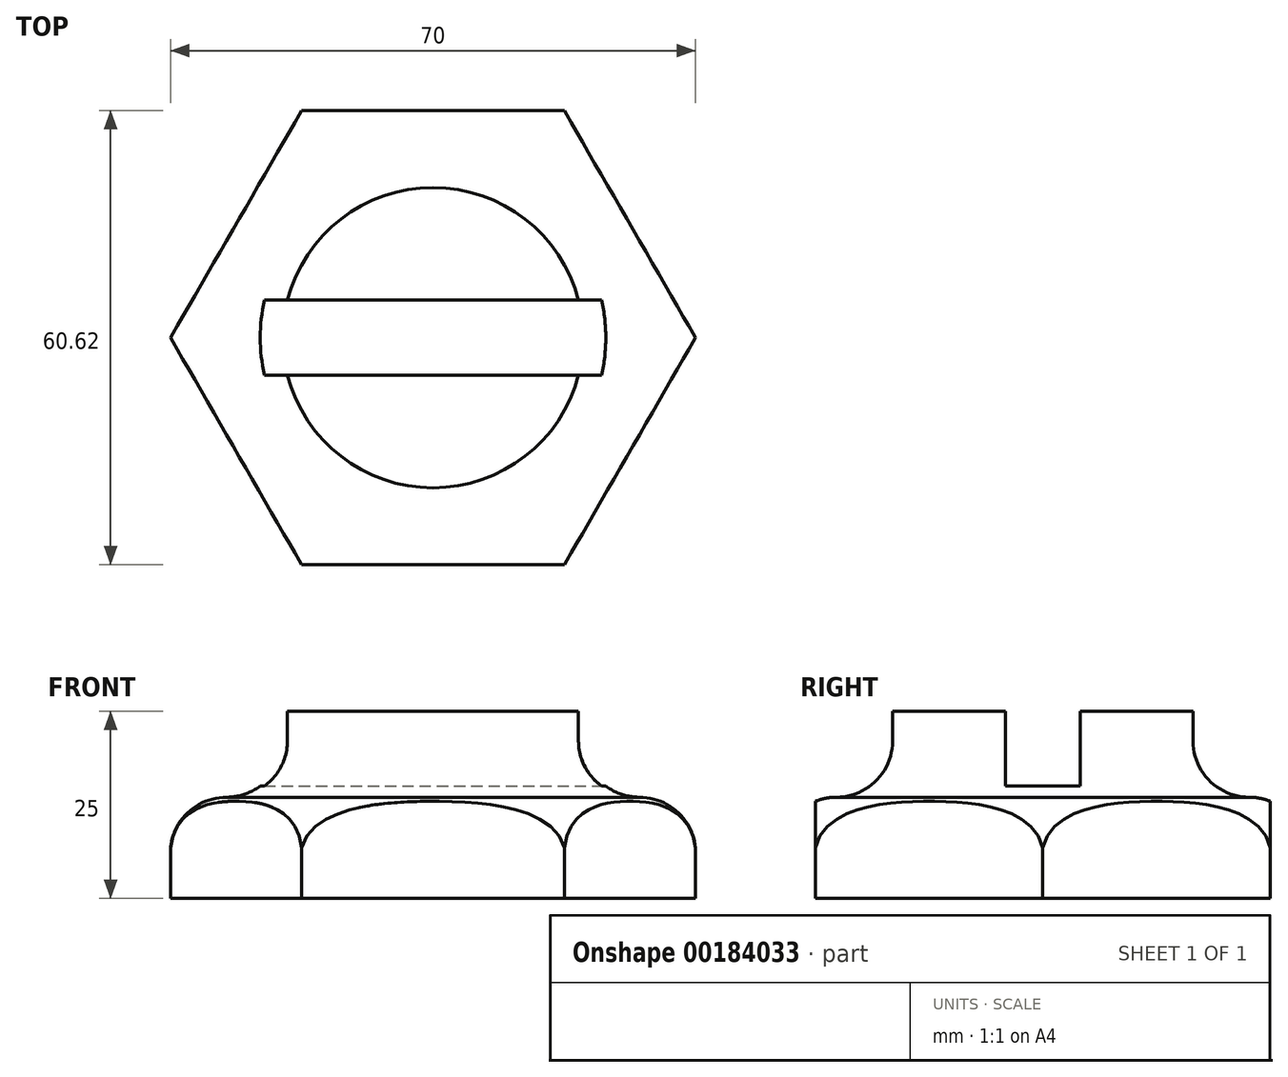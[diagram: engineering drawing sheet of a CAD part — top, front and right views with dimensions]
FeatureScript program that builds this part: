
annotation { "Feature Type Name" : "Feature", "Feature Type Description" : "" }
export const myFeature = defineFeature(function(context is Context, id is Id, definition is map)
    precondition{}
    {
        {
            var Q0;
            Q0=qCreatedBy(makeId("Top.planeOp"),FACE);
            var sketch = newSketch(context, id + "F0", { "sketchPlane" : qUnion([Q0])});
            skCircle(sketch, "E0.cCircle", {"center": v(0, 0) * mm, "radius": 30.31 * mm, "construction": true});
            skLineSegment(sketch, "E0.0", {"start": v(-17.5, 30.31) * mm, "end": v(17.5, 30.31) * mm});
            skLineSegment(sketch, "E0.1", {"start": v(17.5, 30.31) * mm, "end": v(35, 0) * mm});
            skLineSegment(sketch, "E0.2", {"start": v(35, 0) * mm, "end": v(17.5, -30.31) * mm});
            skLineSegment(sketch, "E0.3", {"start": v(17.5, -30.31) * mm, "end": v(-17.5, -30.31) * mm});
            skLineSegment(sketch, "E0.4", {"start": v(-17.5, -30.31) * mm, "end": v(-35, 0) * mm});
            skLineSegment(sketch, "E0.5", {"start": v(-35, 0) * mm, "end": v(-17.5, 30.31) * mm});
            skPoint(sketch, "E0.0.midPoint", {"position": v(0, 30.31) * mm});
            skCircle(sketch, "E1", {"center": v(0, 0) * mm, "radius": 20 * mm});
            skSolve(sketch);
        }
        {
            var Q0;
            Q0=qSketchRegion(id+"F0",true);
            var Q1;
            {var subQ0=sQuery(id+"F0.wireOp",EDGE,"a584e26b-4d0a-449c-a330-dad7efff0bcd.bottom");var subQ1=sQuery(id+"F0.wireOp",EDGE,"E1");var subQ2=makeQuery(id+"F0.imprint","INTERSECT",VERTEX,{"disambiguationData":[OD(0.0)],"derivedFrom":[subQ1,subQ0]});Q1=makeQuery(id+"F0.imprint","IMPRINT",FACE,{"disambiguationData":[TD([[makeQuery(id+"F0.imprint","IMPRINT",EDGE,{"disambiguationData":[TD([[subQ2,-1.0]])],"derivedFrom":subQ1}),1.0]])]});}
            var Q2;
            {var subQ0=sQuery(id+"F0.wireOp",EDGE,"a584e26b-4d0a-449c-a330-dad7efff0bcd.top");var subQ1=sQuery(id+"F0.wireOp",EDGE,"E1");var subQ2=makeQuery(id+"F0.imprint","INTERSECT",VERTEX,{"disambiguationData":[OD(0.0)],"derivedFrom":[subQ1,subQ0]});Q2=makeQuery(id+"F0.imprint","IMPRINT",FACE,{"disambiguationData":[TD([[makeQuery(id+"F0.imprint","IMPRINT",EDGE,{"disambiguationData":[TD([[subQ2,1.0]])],"derivedFrom":subQ1}),1.0]])]});}
            extrude(context, id + "F1", {"entities" : qUnion([Q0, Q1, Q2]), "depth" : 25 * mm});
        }
        {
            var Q0;
            Q0=qCreatedBy(makeId("Front.planeOp"),FACE);
            var sketch = newSketch(context, id + "F2", { "sketchPlane" : qUnion([Q0])});
            skLineSegment(sketch, "E2", {"start": v(-35.04, 0) * mm, "end": v(-35.04, 6) * mm});
            skLineSegment(sketch, "E3", {"start": v(-35.04, 6) * mm, "end": v(-35.04, 24.87) * mm});
            skLineSegment(sketch, "E4", {"start": v(-35.04, 6) * mm, "end": v(-27.54, 6) * mm});
            skArc(sketch, "E5", {"start": v(-27.54, 13.5) * mm, "mid": v(-32.84, 11.3) * mm, "end": v(-35.04, 6) * mm});
            skArc(sketch, "E6", {"start": v(-35, 21.66) * mm, "mid": v(-35.04, 21.01) * mm, "end": v(-35, 20.37) * mm});
            skLineSegment(sketch, "E7.0", {"start": v(-17.5, 25) * mm, "end": v(-35, 25) * mm});
            skLineSegment(sketch, "E8", {"start": v(-20.04, 21) * mm, "end": v(-20.04, 25) * mm});
            skLineSegment(sketch, "E9", {"start": v(-20.04, 25) * mm, "end": v(-35, 25) * mm});
            skLineSegment(sketch, "E10", {"start": v(-35.04, 6) * mm, "end": v(-35, 25) * mm});
            skArc(sketch, "E11.trimOffspring", {"start": v(-27.54, 13.5) * mm, "mid": v(-22.23, 15.7) * mm, "end": v(-20.04, 21) * mm});
            skLineSegment(sketch, "E12", {"start": v(0, 0) * mm, "end": v(0, 43.34) * mm});
            skSolve(sketch);
        }
        {
            var Q0;
            Q0=makeQuery(id+"F2.imprint","IMPRINT",FACE,{"disambiguationData":[TD([[makeQuery(id+"F2.imprint","IMPRINT",EDGE,{"derivedFrom":sQuery(id+"F2.wireOp",EDGE,"E8")}),1.0]])]});
            var Q1;
            Q1=sQuery(id+"F2.wireOp",EDGE,"E12");
            revolve(context, id + "F3", {"operationType" : NewBodyOperationType.REMOVE, "entities" : qUnion([Q0]), "axis" : qUnion([Q1]), "revolveType" : RevolveType.FULL, "oppositeDirection" : true});
        }
        {
            var Q0;
            Q0=makeQuery(id+"F0.imprint","IMPRINT",FACE,{"disambiguationData":[TD([[makeQuery(id+"F0.imprint","IMPRINT",EDGE,{"derivedFrom":sQuery(id+"F0.wireOp",EDGE,"E1")}),1.0]])]});
            extrude(context, id + "F4", {"entities" : qUnion([Q0]), "operationType" : NewBodyOperationType.ADD, "depth" : 25 * mm});
        }
        {
            var Q0;
            Q0=qCreatedBy(makeId("Top.planeOp"),FACE);
            var sketch = newSketch(context, id + "F5", { "sketchPlane" : qUnion([Q0])});
            skLineSegment(sketch, "E13.bottom", {"start": v(-29.77, 0) * mm, "end": v(29.96, 0) * mm});
            skLineSegment(sketch, "E13.top", {"start": v(-29.77, 5.14) * mm, "end": v(29.96, 5.14) * mm});
            skLineSegment(sketch, "E13.left", {"start": v(-29.77, 0) * mm, "end": v(-29.77, 5.14) * mm});
            skLineSegment(sketch, "E13.right", {"start": v(29.96, 0) * mm, "end": v(29.96, 5.14) * mm});
            skSolve(sketch);
        }
        {
            var Q0;
            Q0=makeQuery(id+"F5.imprint","IMPRINT",FACE,{"disambiguationData":[TD([[makeQuery(id+"F5.imprint","IMPRINT",EDGE,{"derivedFrom":sQuery(id+"F5.wireOp",EDGE,"E13.bottom")}),1.0]])]});
            extrude(context, id + "F6", {"entities" : qUnion([Q0]), "operationType" : NewBodyOperationType.ADD, "depth" : 10 * mm});
        }
        {
            var Q0;
            Q0=qCreatedBy(makeId("Right.planeOp"),FACE);
            var sketch = newSketch(context, id + "F7", { "sketchPlane" : qUnion([Q0])});
            skLineSegment(sketch, "E14.0", {"start": v(-20.04, 25) * mm, "end": v(20.04, 25) * mm});
            skLineSegment(sketch, "E15", {"start": v(0, 25) * mm, "end": v(5, 25) * mm});
            skLineSegment(sketch, "E16", {"start": v(5, 25) * mm, "end": v(5, 15) * mm});
            skLineSegment(sketch, "E17", {"start": v(5, 15) * mm, "end": v(-5, 15) * mm});
            skLineSegment(sketch, "E18", {"start": v(-5, 15) * mm, "end": v(-5, 25) * mm});
            skLineSegment(sketch, "E19", {"start": v(-5, 25) * mm, "end": v(0, 25) * mm});
            skSolve(sketch);
        }
        {
            var Q0;
            Q0 = qSketchRegion(id + "F7", true);
            extrude(context, id + "F8", {"entities" : qUnion([Q0]), "operationType" : NewBodyOperationType.REMOVE, "endBound" : BoundingType.SYMMETRIC, "oppositeDirection" : true, "depth" : 200 * mm});
        }
    });
